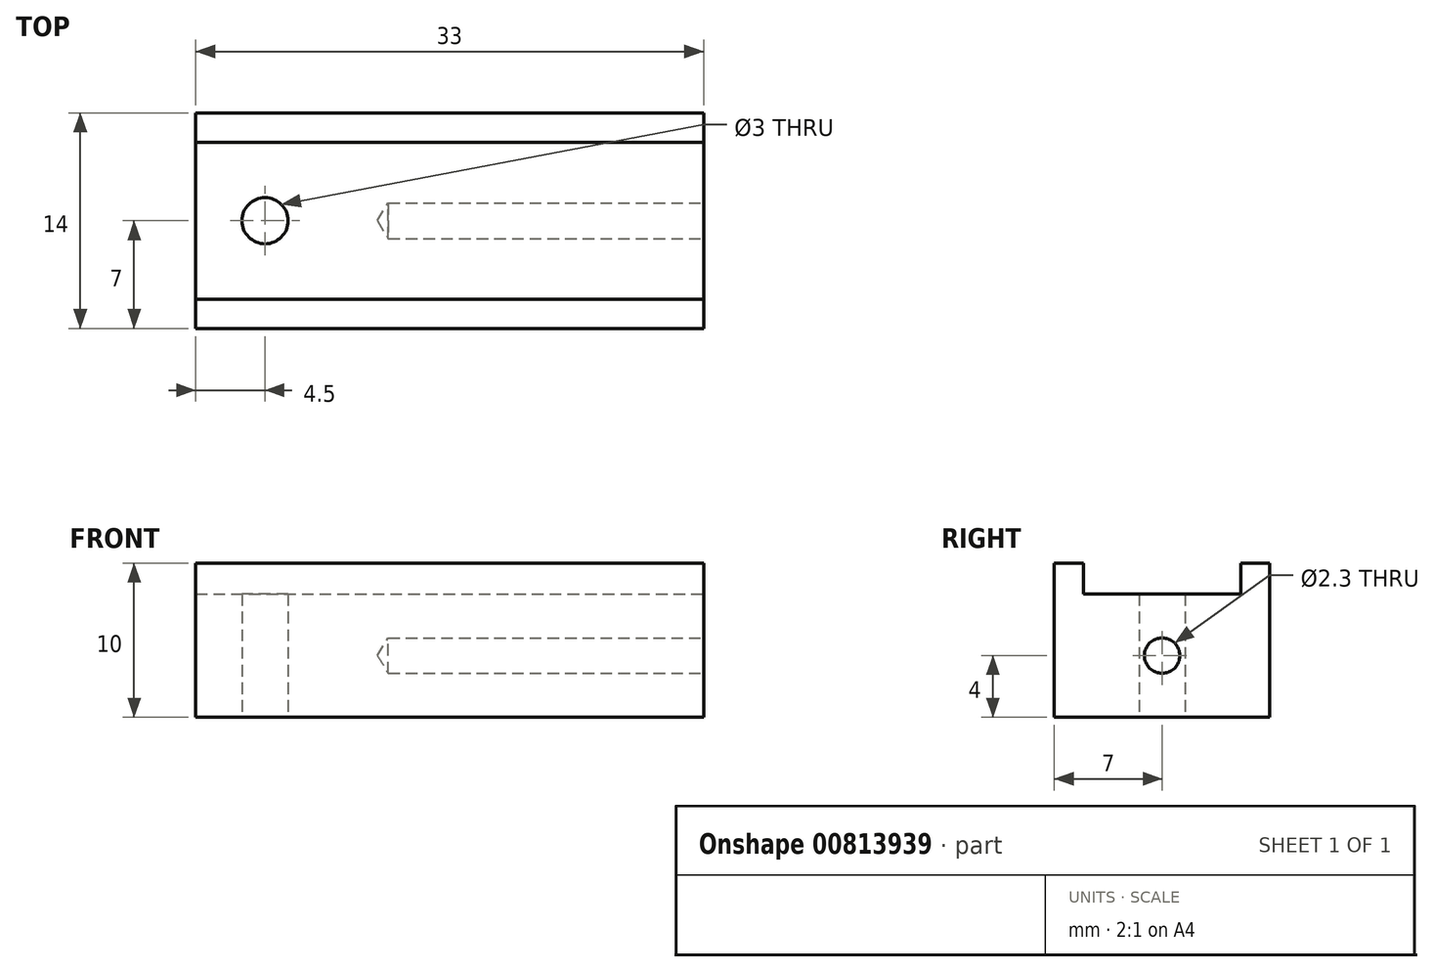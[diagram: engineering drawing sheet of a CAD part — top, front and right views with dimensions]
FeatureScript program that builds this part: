
annotation { "Feature Type Name" : "Feature", "Feature Type Description" : "" }
export const myFeature = defineFeature(function(context is Context, id is Id, definition is map)
    precondition{}
    {
        {
            var Q0;
            Q0=qCreatedBy(makeId("Top.planeOp"),FACE);
            var sketch = newSketch(context, id + "F0", { "sketchPlane" : qUnion([Q0])});
            skLineSegment(sketch, "E0.bottom", {"start": v(-16.5, 7) * mm, "end": v(16.5, 7) * mm});
            skLineSegment(sketch, "E0.top", {"start": v(-16.5, -7) * mm, "end": v(16.5, -7) * mm});
            skLineSegment(sketch, "E0.left", {"start": v(-16.5, 7) * mm, "end": v(-16.5, -7) * mm});
            skLineSegment(sketch, "E0.right", {"start": v(16.5, 7) * mm, "end": v(16.5, -7) * mm});
            skPoint(sketch, "E1", {"position": v(12, 0) * mm});
            skPoint(sketch, "E2", {"position": v(-12, 0) * mm});
            skSolve(sketch);
        }
        {
            var Q0;
            Q0 = qSketchRegion(id + "F0", true);
            extrude(context, id + "F1", {"entities" : qUnion([Q0]), "depth" : 10 * mm, "offsetDistance" : 25 * mm});
        }
        {
            var Q0;
            Q0=makeQuery(id+"F1.opExtrude","CAP_FACE",FACE,{"disambiguationData":[OSD([sQuery(id+"F0.wireOp",EDGE,"E0.bottom"),sQuery(id+"F0.wireOp",EDGE,"E0.top"),sQuery(id+"F0.wireOp",EDGE,"E0.left"),sQuery(id+"F0.wireOp",EDGE,"E0.right")])],"isStart":false});
            var sketch = newSketch(context, id + "F2", { "sketchPlane" : qUnion([Q0])});
            skLineSegment(sketch, "E3.bottom", {"start": v(-16.5, 5.1) * mm, "end": v(16.5, 5.1) * mm});
            skLineSegment(sketch, "E3.top", {"start": v(-16.5, -5.1) * mm, "end": v(16.5, -5.1) * mm});
            skLineSegment(sketch, "E3.left", {"start": v(-16.5, 5.1) * mm, "end": v(-16.5, -5.1) * mm});
            skLineSegment(sketch, "E3.right", {"start": v(16.5, 5.1) * mm, "end": v(16.5, -5.1) * mm});
            skSolve(sketch);
        }
        {
            var Q0;
            Q0=makeQuery(id+"F2.imprint","IMPRINT",FACE,{"disambiguationData":[TD([[makeQuery(id+"F2.imprint","IMPRINT",EDGE,{"derivedFrom":sQuery(id+"F2.wireOp",EDGE,"E3.bottom")}),-1.0]])]});
            extrude(context, id + "F3", {"entities" : qUnion([Q0]), "operationType" : NewBodyOperationType.REMOVE, "oppositeDirection" : true, "depth" : 2 * mm, "offsetDistance" : 25 * mm});
        }
        {
            var Q0;
            Q0=sQuery(id+"F0.wireOp",VERTEX,"E2");
            var Q1;
            Q1=makeQuery(id+"F1.opExtrude","SWEPT_BODY",BODY,{"disambiguationData":[OSD([sQuery(id+"F0.wireOp",EDGE,"E0.bottom"),sQuery(id+"F0.wireOp",EDGE,"E0.top"),sQuery(id+"F0.wireOp",EDGE,"E0.left"),sQuery(id+"F0.wireOp",EDGE,"E0.right")])]});
            hole(context, id + "F4", {"style" : HoleStyle.SIMPLE, "endStyle" : HoleEndStyle.BLIND, "oppositeDirection" : true, "holeDiameter" : 3 * mm, "majorDiameter" : 5 * mm, "holeDepth" : 20.5 * mm, "isTappedThrough" : true, "tappedDepth" : 12 * mm, "tapClearance" : 3, "startFromSketch" : true, "locations" : qUnion([Q0]), "scope" : qUnion([Q1])});
        }
        {
            var Q0;
            Q0=makeQuery(id+"F1.opExtrude","SWEPT_FACE",FACE,{"disambiguationData":[OSD([sQuery(id+"F0.wireOp",EDGE,"E0.right")])]});
            var sketch = newSketch(context, id + "F5", { "sketchPlane" : qUnion([Q0])});
            skPoint(sketch, "E4", {"position": v(0, 4) * mm});
            skSolve(sketch);
        }
        {
            var Q0;
            Q0=sQuery(id+"F5.wireOp",VERTEX,"E4");
            var Q1;
            Q1=makeQuery(id+"F1.opExtrude","SWEPT_BODY",BODY,{"disambiguationData":[OSD([sQuery(id+"F0.wireOp",EDGE,"E0.bottom"),sQuery(id+"F0.wireOp",EDGE,"E0.top"),sQuery(id+"F0.wireOp",EDGE,"E0.left"),sQuery(id+"F0.wireOp",EDGE,"E0.right")])]});
            hole(context, id + "F6", {"style" : HoleStyle.SIMPLE, "endStyle" : HoleEndStyle.BLIND, "holeDiameter" : 2.3 * mm, "majorDiameter" : 5 * mm, "holeDepth" : 20.5 * mm, "isTappedThrough" : true, "tappedDepth" : 12 * mm, "tapClearance" : 3, "startFromSketch" : true, "locations" : qUnion([Q0]), "scope" : qUnion([Q1])});
        }
    });
